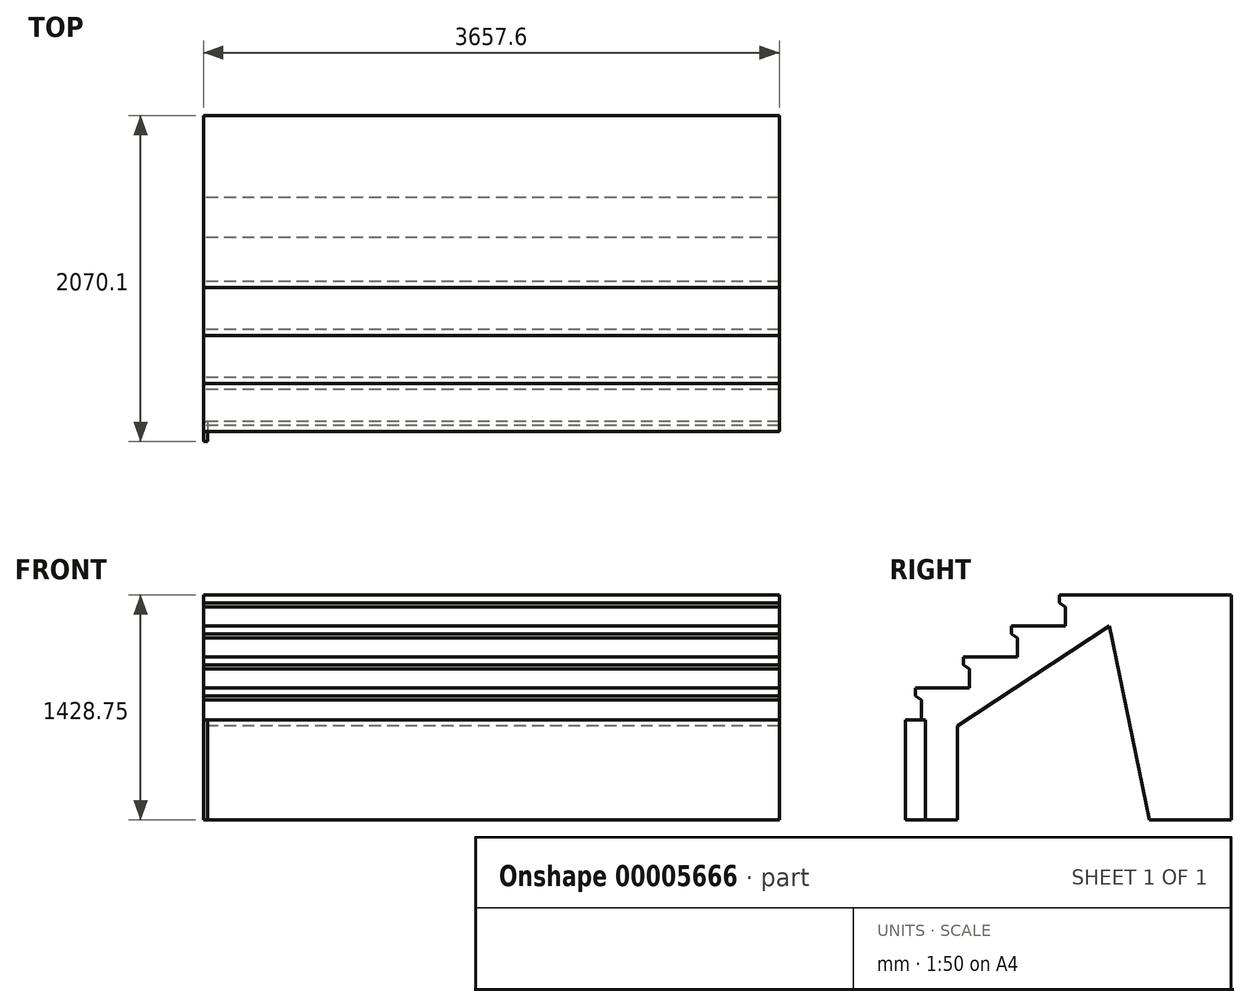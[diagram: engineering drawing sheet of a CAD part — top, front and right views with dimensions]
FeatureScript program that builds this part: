
annotation { "Feature Type Name" : "Feature", "Feature Type Description" : "" }
export const myFeature = defineFeature(function(context is Context, id is Id, definition is map)
    precondition{}
    {
        {
            var Q0;
            Q0=qCreatedBy(makeId("Right.planeOp"),FACE);
            var sketch = newSketch(context, id + "F0", { "sketchPlane" : qUnion([Q0])});
            skLineSegment(sketch, "E0.bottom", {"start": v(0, 0) * mm, "end": v(203.76, 0) * mm});
            skLineSegment(sketch, "E0.top", {"start": v(0, 838.2) * mm, "end": v(203.76, 838.2) * mm});
            skLineSegment(sketch, "E0.left", {"start": v(0, 0) * mm, "end": v(0, 635) * mm});
            skLineSegment(sketch, "E0.right", {"start": v(203.76, 0) * mm, "end": v(203.76, 596.9) * mm});
            skLineSegment(sketch, "E1.bottom", {"start": v(0, 838.2) * mm, "end": v(-25.4, 838.2) * mm});
            skLineSegment(sketch, "E1.top", {"start": v(0, 635) * mm, "end": v(-25.4, 635) * mm});
            skLineSegment(sketch, "E2.bottom", {"start": v(-25.4, 838.2) * mm, "end": v(279.4, 838.2) * mm});
            skLineSegment(sketch, "E3.top", {"start": v(279.4, 1035.05) * mm, "end": v(584.2, 1035.05) * mm});
            skLineSegment(sketch, "E3.left", {"start": v(279.4, 838.2) * mm, "end": v(279.4, 958.85) * mm});
            skLineSegment(sketch, "E4.top", {"start": v(584.2, 1231.9) * mm, "end": v(889, 1231.9) * mm});
            skLineSegment(sketch, "E4.left", {"start": v(584.2, 1035.05) * mm, "end": v(584.2, 1155.7) * mm});
            skLineSegment(sketch, "E5.bottom", {"start": v(-25.4, 838.2) * mm, "end": v(-63.5, 838.2) * mm});
            skLineSegment(sketch, "E5.right", {"start": v(-63.5, 838.2) * mm, "end": v(-63.5, 787.4) * mm});
            skLineSegment(sketch, "E6", {"start": v(-63.5, 787.4) * mm, "end": v(-25.4, 762) * mm});
            skLineSegment(sketch, "E7.bottom", {"start": v(279.4, 1035.05) * mm, "end": v(241.3, 1035.05) * mm});
            skLineSegment(sketch, "E7.right", {"start": v(241.3, 1035.05) * mm, "end": v(241.3, 984.25) * mm});
            skLineSegment(sketch, "E8", {"start": v(241.3, 984.25) * mm, "end": v(279.4, 958.85) * mm});
            skLineSegment(sketch, "E9", {"start": v(1168.4, 1231.9) * mm, "end": v(1422.96, 0) * mm});
            skLineSegment(sketch, "E10", {"start": v(1168.4, 1231.9) * mm, "end": v(203.76, 596.9) * mm});
            skLineSegment(sketch, "E11.top", {"start": v(889, 1428.75) * mm, "end": v(1193.8, 1428.75) * mm});
            skLineSegment(sketch, "E11.left", {"start": v(889, 1231.9) * mm, "end": v(889, 1352.55) * mm});
            skLineSegment(sketch, "E12.bottom", {"start": v(889, 1428.75) * mm, "end": v(850.9, 1428.75) * mm});
            skLineSegment(sketch, "E12.right", {"start": v(850.9, 1428.75) * mm, "end": v(850.9, 1377.95) * mm});
            skLineSegment(sketch, "E13.bottom", {"start": v(584.2, 1231.9) * mm, "end": v(546.1, 1231.9) * mm});
            skLineSegment(sketch, "E13.right", {"start": v(546.1, 1231.9) * mm, "end": v(546.1, 1181.1) * mm});
            skLineSegment(sketch, "E14", {"start": v(850.9, 1377.95) * mm, "end": v(889, 1352.55) * mm});
            skLineSegment(sketch, "E15", {"start": v(546.1, 1181.1) * mm, "end": v(584.2, 1155.7) * mm});
            skLineSegment(sketch, "E16.bottom", {"start": v(850.9, 1428.75) * mm, "end": v(1193.8, 1428.75) * mm});
            skLineSegment(sketch, "E17.left", {"start": v(1943.1, 1428.75) * mm, "end": v(1943.1, 0) * mm});
            skLineSegment(sketch, "E18", {"start": v(1422.96, 0) * mm, "end": v(1943.1, 0) * mm});
            skLineSegment(sketch, "E19", {"start": v(1943.1, 1428.75) * mm, "end": v(1193.8, 1428.75) * mm});
            skLineSegment(sketch, "E20.trimOffspring", {"start": v(-25.4, 762) * mm, "end": v(-25.4, 635) * mm});
            skSolve(sketch);
        }
        {
            var Q0;
            Q0=makeQuery(id+"F0.imprint","IMPRINT",FACE,{"disambiguationData":[TD([[makeQuery(id+"F0.imprint","IMPRINT",EDGE,{"derivedFrom":sQuery(id+"F0.wireOp",EDGE,"E0.bottom")}),1.0]])]});
            extrude(context, id + "F1", {"entities" : qUnion([Q0]), "depth" : 3657.6 * mm});
        }
        {
            var Q0;
            Q0=qCreatedBy(makeId("Top.planeOp"),FACE);
            var sketch = newSketch(context, id + "F2", { "sketchPlane" : qUnion([Q0])});
            skLineSegment(sketch, "E21.bottom", {"start": v(0, 0) * mm, "end": v(25.4, 0) * mm});
            skLineSegment(sketch, "E21.top", {"start": v(0, -127) * mm, "end": v(25.4, -127) * mm});
            skLineSegment(sketch, "E21.left", {"start": v(0, 0) * mm, "end": v(0, -127) * mm});
            skLineSegment(sketch, "E21.right", {"start": v(25.4, 0) * mm, "end": v(25.4, -127) * mm});
            skSolve(sketch);
        }
        {
            var Q0;
            Q0=makeQuery(id+"F2.imprint","IMPRINT",FACE,{"disambiguationData":[TD([[makeQuery(id+"F2.imprint","IMPRINT",EDGE,{"derivedFrom":sQuery(id+"F2.wireOp",EDGE,"E21.bottom")}),-1.0]])]});
            extrude(context, id + "F3", {"entities" : qUnion([Q0]), "depth" : 635 * mm});
        }
    });
